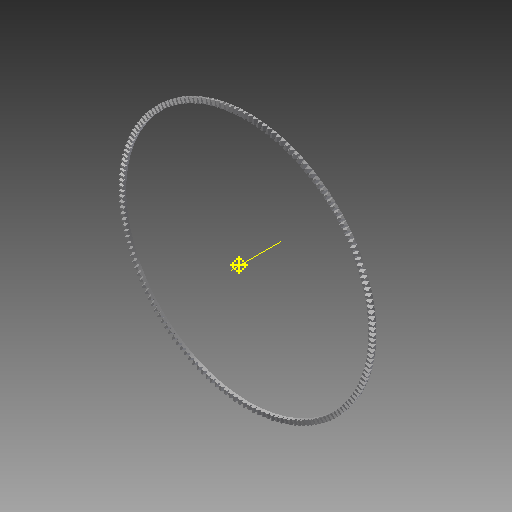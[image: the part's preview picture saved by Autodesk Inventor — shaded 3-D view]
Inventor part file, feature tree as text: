
AUTODESK INVENTOR PART (.ipt)
format: ipt  version: 2017 (Build 210142000, 142)  size: 2,307,072 bytes
history: native  units: mm
features: other x24, loft x2, pattern_circular x2, sketch x2, extrude x1
ambient origin geometry x6: Origin, XZ Plane, X Axis, Y Axis, Z Axis, Center Point
bodies: Solid1 (feature_tree)
feature tree (31):
  other  "Top Point"
  other  "Mesh Plane2"
  other  "Teeth Body"
  other  "Start Point"
  other  "Tooth Plane"
  other  "Start Sketch"
  other  "End Point"
  other  "3D Sketch Right"
  other  "End Plane Right"
  loft  "Loft Right"
  pattern_circular  "Circular Pattern Right"  [2 undecoded]
  other  "3D Sketch Left"
  other  "End Plane Left"
  loft  "Loft Left"
  pattern_circular  "Circular Pattern Left"  Angle=90.0deg  [1 undecoded]
  other  "Fix Body"
  extrude  "Extrusion1"  Depth=10.0mm
  other  "Mesh Plane"
  other  "Top Plane"
  other  "Teeth Body Sketch"
  other  "End Plane"
  other  "End Sketch"
  other  "Helical Curve Left"
  other  "End Sketch Left"
  other  "Body Sketch"
  sketch  "Sketch6"  dims[d0=284.48mm d1=284.160291mm]
  other  "Srf1"
  other  "Helical Curve Right"
  other  "End Sketch Right"
  sketch  "Sketch8"  dims[d2=284.691129mm d3=5.08mm d4=8.682099mm d5=90.0deg d7=843.709239mm d8=773.363113mm d9=1655.912975mm d11=5.266267mm d12=813.395001mm d15=745.576392mm d16=1596.416484mm d17=0.0mm d18=90.0deg d19=0.0mm d20=90.0deg d21=1680.0mm d22=360.0deg d26=126.354884mm d27=0.375206mm d28=284.48mm d29=-14.994889mm d30=813.395001mm d31=745.576392mm d32=1596.416484mm d35=0.0mm d37=0.0mm d39=0.0mm d40=90.0deg d41=1680.0mm d42=360.0deg d46=90.0deg d47=90.0deg d48=0.0mm d49=0.0mm d50=90.0deg d51=0.187mm d52=0.0mm d53=0.0mm d54=0.0mm d56=9.831614mm d57=1999.032804mm d58=1993.742831mm d59=1927.208114mm d60=1922.108207mm d61=1927.208114mm d62=1922.108207mm d63=90.0deg d64=90.0deg d65=126.354884mm d66=31.5mm d67=284.48mm d68=-14.994889mm d69=0.375206mm d70=745.576392mm d71=1596.416484mm d72=813.395001mm d73=1922.108207mm d74=1927.208114mm d75=0.0mm d76=90.0deg d77=0.0mm d78=90.0deg d79=0.0mm d80=90.0deg d81=1680.0mm d82=360.0deg d84=10.0mm d85=20.0mm d86=20.0mm d87=10.0mm d88=0.0mm d89=0.0mm d90=25.4mm d91=0.0mm]
  other  "Pitch Diameter"
note: 3 required parameter values undecoded (feature->parameter linkage not recoverable at this tier; creation-order binding heuristic only, values carry confidence <= 0.55)
